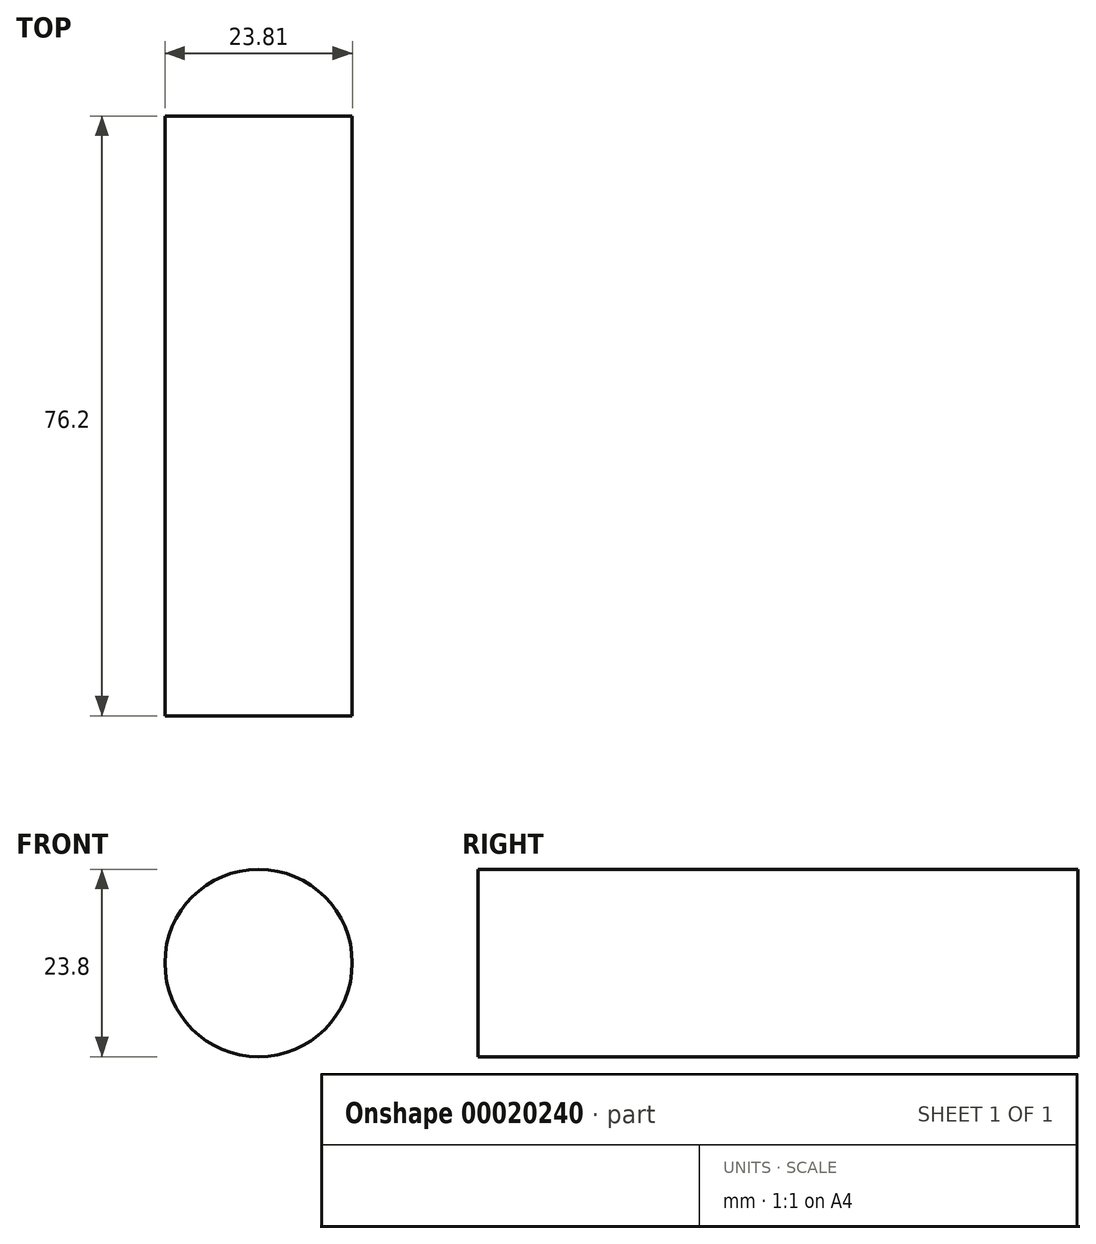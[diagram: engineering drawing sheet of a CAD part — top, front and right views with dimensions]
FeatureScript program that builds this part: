
annotation { "Feature Type Name" : "Feature", "Feature Type Description" : "" }
export const myFeature = defineFeature(function(context is Context, id is Id, definition is map)
    precondition{}
    {
        {
            var Q0;
            Q0=qCreatedBy(makeId("Front.planeOp"),FACE);
            var sketch = newSketch(context, id + "F0", { "sketchPlane" : qUnion([Q0])});
            skLineSegment(sketch, "E0", {"start": v(-26.81, 32.45) * mm, "end": v(14.32, 32.45) * mm});
            skLineSegment(sketch, "E1", {"start": v(14.32, 32.45) * mm, "end": v(14.32, 0) * mm});
            skLineSegment(sketch, "E2", {"start": v(14.32, 0) * mm, "end": v(-26.44, 0) * mm});
            skCircle(sketch, "E3", {"center": v(-6.94, 16.3) * mm, "radius": 11.9 * mm});
            skSolve(sketch);
        }
        {
            var Q0;
            Q0 = qSketchRegion(id + "F0", true);
            extrude(context, id + "F1", {"entities" : qUnion([Q0]), "depth" : 76.2 * mm});
        }
    });
